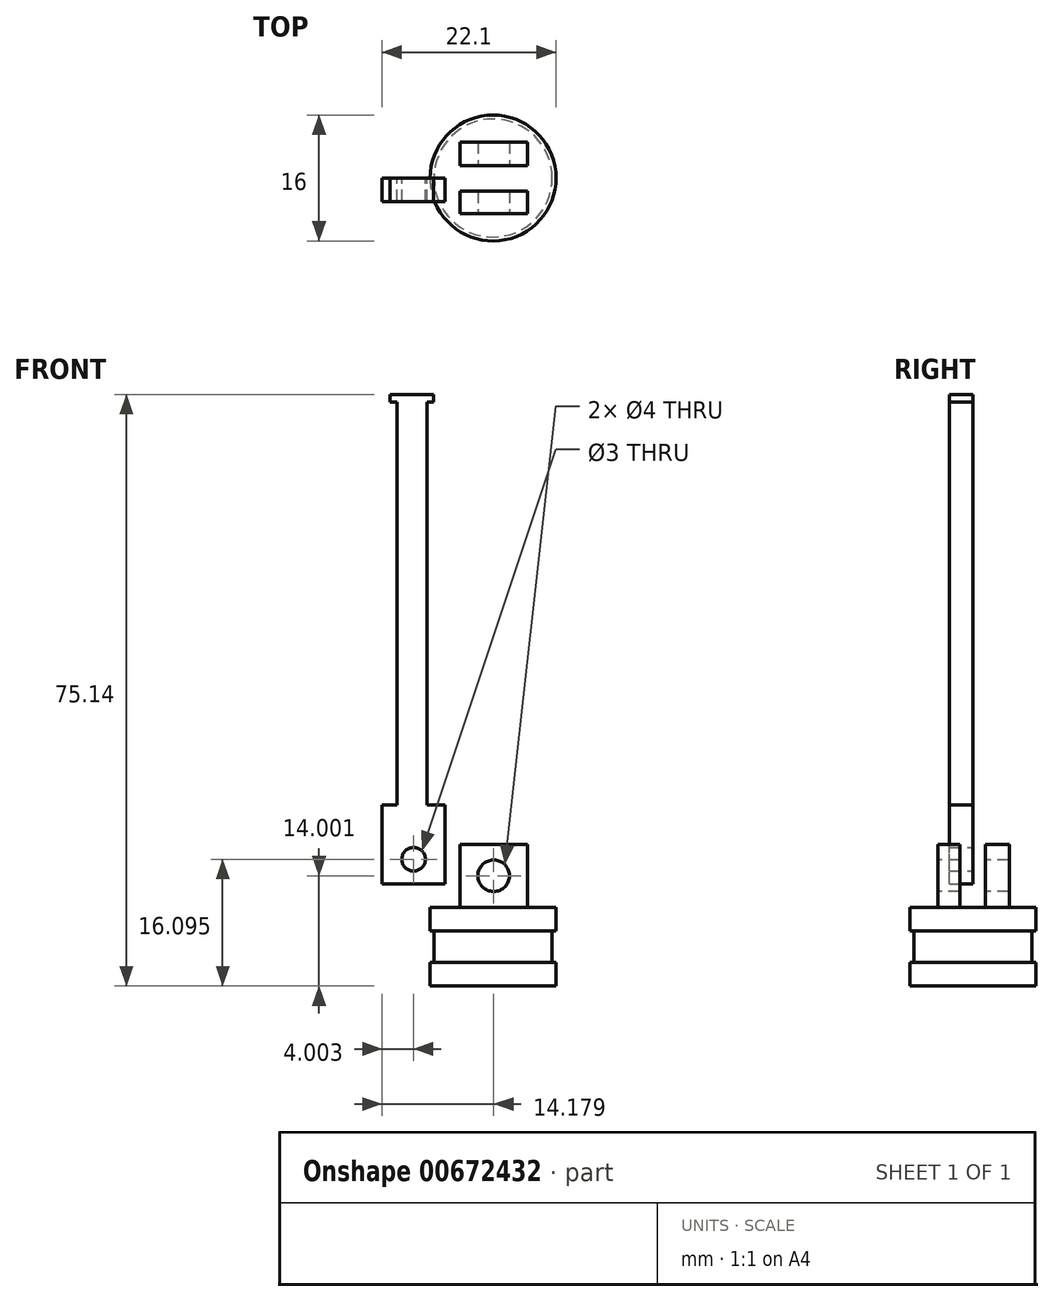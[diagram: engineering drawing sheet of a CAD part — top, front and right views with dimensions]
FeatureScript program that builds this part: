
annotation { "Feature Type Name" : "Feature", "Feature Type Description" : "" }
export const myFeature = defineFeature(function(context is Context, id is Id, definition is map)
    precondition{}
    {
        {
            var Q0;
            Q0=qCreatedBy(makeId("Front.planeOp"),FACE);
            var sketch = newSketch(context, id + "F0", { "sketchPlane" : qUnion([Q0])});
            skLineSegment(sketch, "E0", {"start": v(0, 8.53) * mm, "end": v(-8, 8.53) * mm});
            skLineSegment(sketch, "E1", {"start": v(-8, 8.53) * mm, "end": v(-8, 5.53) * mm});
            skLineSegment(sketch, "E2", {"start": v(-8, 5.53) * mm, "end": v(-7.5, 5.53) * mm});
            skLineSegment(sketch, "E3", {"start": v(-7.5, 5.53) * mm, "end": v(-7.5, 1.53) * mm});
            skLineSegment(sketch, "E4", {"start": v(-7.5, 1.53) * mm, "end": v(-8, 1.53) * mm});
            skLineSegment(sketch, "E5", {"start": v(-8, 1.53) * mm, "end": v(-8, -1.47) * mm});
            skLineSegment(sketch, "E6", {"start": v(-8, -1.47) * mm, "end": v(0, -1.47) * mm});
            skLineSegment(sketch, "E7", {"start": v(0, -1.47) * mm, "end": v(0, 8.53) * mm});
            skSolve(sketch);
        }
        {
            var Q0;
            Q0=makeQuery(id+"F0.imprint","IMPRINT",FACE,{"disambiguationData":[TD([[makeQuery(id+"F0.imprint","IMPRINT",EDGE,{"derivedFrom":sQuery(id+"F0.wireOp",EDGE,"E0")}),1.0]])]});
            var Q1;
            Q1=sQuery(id+"F0.wireOp",EDGE,"E7");
            revolve(context, id + "F1", {"entities" : qUnion([Q0]), "axis" : qUnion([Q1]), "revolveType" : RevolveType.FULL});
        }
        {
            var Q0;
            Q0=makeQuery(id+"F1.opRevolve","SWEPT_FACE",FACE,{"disambiguationData":[OSD([sQuery(id+"F0.wireOp",EDGE,"E0")])]});
            var sketch = newSketch(context, id + "F2", { "sketchPlane" : qUnion([Q0])});
            skLineSegment(sketch, "E8.bottom", {"start": v(-3, -4.5) * mm, "end": v(6, -4.5) * mm});
            skLineSegment(sketch, "E8.top", {"start": v(-2.71, 4.59) * mm, "end": v(6, 4.59) * mm});
            skLineSegment(sketch, "E9", {"start": v(-3, -1.67) * mm, "end": v(6, -1.67) * mm});
            skLineSegment(sketch, "E10", {"start": v(-2.71, 1.59) * mm, "end": v(6, 1.59) * mm});
            skLineSegment(sketch, "E11", {"start": v(4.37, -4.5) * mm, "end": v(4.37, -1.67) * mm});
            skLineSegment(sketch, "E12", {"start": v(4.37, 1.59) * mm, "end": v(4.37, 4.59) * mm});
            skLineSegment(sketch, "E13", {"start": v(-2.71, 4.59) * mm, "end": v(-4.21, 4.59) * mm});
            skLineSegment(sketch, "E14", {"start": v(-4.21, 4.59) * mm, "end": v(-4.21, 1.59) * mm});
            skLineSegment(sketch, "E15", {"start": v(-4.21, 1.59) * mm, "end": v(-2.71, 1.59) * mm});
            skLineSegment(sketch, "E16", {"start": v(-3, -1.67) * mm, "end": v(-4.21, -1.67) * mm});
            skLineSegment(sketch, "E17", {"start": v(-4.21, -1.67) * mm, "end": v(-4.21, -4.5) * mm});
            skLineSegment(sketch, "E18", {"start": v(-4.21, -4.5) * mm, "end": v(-3, -4.5) * mm});
            skSolve(sketch);
        }
        {
            var Q0;
            Q0=makeQuery(id+"F2.imprint","IMPRINT",FACE,{"disambiguationData":[TD([[makeQuery(id+"F2.imprint","IMPRINT",EDGE,{"derivedFrom":sQuery(id+"F2.wireOp",EDGE,"E8.bottom")}),1.0]])]});
            var Q1;
            {var subQ0=sQuery(id+"F2.wireOp",EDGE,"E8.top");Q1=makeQuery(id+"F2.imprint","IMPRINT",FACE,{"disambiguationData":[TD([[makeQuery(id+"F2.imprint","IMPRINT",EDGE,{"derivedFrom":subQ0}),-1.0]])]});}
            extrude(context, id + "F3", {"entities" : qUnion([Q0, Q1]), "operationType" : NewBodyOperationType.ADD, "depth" : 8 * mm, "offsetDistance" : 25 * mm});
        }
        {
            var Q0;
            Q0=makeQuery(id+"F3.opExtrude","SWEPT_FACE",FACE,{"disambiguationData":[OSD([sQuery(id+"F2.wireOp",EDGE,"E8.bottom")])]});
            var sketch = newSketch(context, id + "F4", { "sketchPlane" : qUnion([Q0])});
            skPoint(sketch, "E19", {"position": v(0.08, 12.53) * mm});
            skPoint(sketch, "E19.positionSnap0", {"position": v(0.08, 16.53) * mm});
            skPoint(sketch, "E19.positionSnap1", {"position": v(4.37, 12.53) * mm});
            skSolve(sketch);
        }
        {
            var Q0;
            Q0=sQuery(id+"F4.wireOp",VERTEX,"E19");
            var Q1;
            Q1=makeQuery(id+"F1.opRevolve","SWEPT_BODY",BODY,{"disambiguationData":[OSD([sQuery(id+"F0.wireOp",EDGE,"E0"),sQuery(id+"F0.wireOp",EDGE,"E1"),sQuery(id+"F0.wireOp",EDGE,"E2"),sQuery(id+"F0.wireOp",EDGE,"E3"),sQuery(id+"F0.wireOp",EDGE,"E4"),sQuery(id+"F0.wireOp",EDGE,"E5"),sQuery(id+"F0.wireOp",EDGE,"E6"),sQuery(id+"F0.wireOp",EDGE,"E7")])]});
            hole(context, id + "F5", {"style" : HoleStyle.SIMPLE, "endStyle" : HoleEndStyle.THROUGH, "holeDiameter" : 4 * mm, "majorDiameter" : 5 * mm, "isTappedThrough" : true, "tappedDepth" : 12 * mm, "tapClearance" : 3, "startFromSketch" : true, "locations" : qUnion([Q0]), "scope" : qUnion([Q1])});
        }
        {
            var Q0;
            Q0=qCreatedBy(makeId("Front.planeOp"),FACE);
            var sketch = newSketch(context, id + "F6", { "sketchPlane" : qUnion([Q0])});
            skLineSegment(sketch, "E20.bottom", {"start": v(-6.1, 11.52) * mm, "end": v(-14.1, 11.52) * mm});
            skLineSegment(sketch, "E20.top", {"start": v(-6.1, 21.52) * mm, "end": v(-14.1, 21.52) * mm});
            skLineSegment(sketch, "E20.left", {"start": v(-6.1, 11.52) * mm, "end": v(-6.1, 21.52) * mm});
            skLineSegment(sketch, "E20.right", {"start": v(-14.1, 11.52) * mm, "end": v(-14.1, 21.52) * mm});
            skPoint(sketch, "E21", {"position": v(-10.1, 16.52) * mm});
            skPoint(sketch, "E21.positionSnap0", {"position": v(-10.1, 11.52) * mm});
            skPoint(sketch, "E21.positionSnap1", {"position": v(-6.1, 16.52) * mm});
            skLineSegment(sketch, "E22", {"start": v(-8.42, 21.52) * mm, "end": v(-8.42, 72.7) * mm});
            skLineSegment(sketch, "E23", {"start": v(-8.42, 72.7) * mm, "end": v(-12.2, 72.7) * mm});
            skLineSegment(sketch, "E24", {"start": v(-12.2, 72.7) * mm, "end": v(-12.2, 21.52) * mm});
            skLineSegment(sketch, "E25.bottom", {"start": v(-8.42, 72.7) * mm, "end": v(-13.12, 72.7) * mm});
            skLineSegment(sketch, "E25.top", {"start": v(-8.42, 73.67) * mm, "end": v(-13.12, 73.67) * mm});
            skLineSegment(sketch, "E25.left", {"start": v(-8.42, 72.7) * mm, "end": v(-8.42, 73.67) * mm});
            skLineSegment(sketch, "E25.right", {"start": v(-13.12, 72.7) * mm, "end": v(-13.12, 73.67) * mm});
            skLineSegment(sketch, "E26.bottom", {"start": v(-8.42, 72.7) * mm, "end": v(-7.57, 72.7) * mm});
            skLineSegment(sketch, "E26.top", {"start": v(-8.42, 73.67) * mm, "end": v(-7.57, 73.67) * mm});
            skLineSegment(sketch, "E26.right", {"start": v(-7.57, 72.7) * mm, "end": v(-7.57, 73.67) * mm});
            skSolve(sketch);
        }
        {
            var Q0;
            Q0 = qSketchRegion(id + "F6", true);
            extrude(context, id + "F7", {"entities" : qUnion([Q0]), "depth" : 3 * mm, "offsetDistance" : 25 * mm});
        }
        {
            var Q0;
            Q0=makeQuery(id+"F7.opExtrude","CAP_FACE",FACE,{"disambiguationData":[OSD([sQuery(id+"F6.wireOp",EDGE,"E20.bottom"),sQuery(id+"F6.wireOp",EDGE,"E20.top"),sQuery(id+"F6.wireOp",EDGE,"E20.left"),sQuery(id+"F6.wireOp",EDGE,"E20.right"),sQuery(id+"F6.wireOp",EDGE,"E22"),sQuery(id+"F6.wireOp",EDGE,"E24"),sQuery(id+"F6.wireOp",EDGE,"E25.bottom"),sQuery(id+"F6.wireOp",EDGE,"E25.top"),sQuery(id+"F6.wireOp",EDGE,"E25.right"),sQuery(id+"F6.wireOp",EDGE,"E26.bottom"),sQuery(id+"F6.wireOp",EDGE,"E26.top"),sQuery(id+"F6.wireOp",EDGE,"E26.right")])],"isStart":true});
            var sketch = newSketch(context, id + "F8", { "sketchPlane" : qUnion([Q0])});
            skPoint(sketch, "E27", {"position": v(10.1, 16.52) * mm});
            skPoint(sketch, "E27.positionSnap0", {"position": v(10.1, 11.52) * mm});
            skPoint(sketch, "E27.positionSnap1", {"position": v(6.1, 16.52) * mm});
            skPoint(sketch, "E28", {"position": v(10.1, 14.63) * mm});
            skSolve(sketch);
        }
        {
            var Q0;
            Q0=sQuery(id+"F8.wireOp",VERTEX,"E28");
            var Q1;
            Q1=makeQuery(id+"F7.opExtrude","SWEPT_BODY",BODY,{"disambiguationData":[OSD([sQuery(id+"F6.wireOp",EDGE,"E20.bottom"),sQuery(id+"F6.wireOp",EDGE,"E20.top"),sQuery(id+"F6.wireOp",EDGE,"E20.left"),sQuery(id+"F6.wireOp",EDGE,"E20.right"),sQuery(id+"F6.wireOp",EDGE,"E22"),sQuery(id+"F6.wireOp",EDGE,"E24"),sQuery(id+"F6.wireOp",EDGE,"E25.bottom"),sQuery(id+"F6.wireOp",EDGE,"E25.top"),sQuery(id+"F6.wireOp",EDGE,"E25.right"),sQuery(id+"F6.wireOp",EDGE,"E26.bottom"),sQuery(id+"F6.wireOp",EDGE,"E26.top"),sQuery(id+"F6.wireOp",EDGE,"E26.right")])]});
            hole(context, id + "F9", {"style" : HoleStyle.SIMPLE, "endStyle" : HoleEndStyle.THROUGH, "holeDiameter" : 3 * mm, "majorDiameter" : 5 * mm, "isTappedThrough" : true, "tappedDepth" : 12 * mm, "tapClearance" : 3, "startFromSketch" : true, "locations" : qUnion([Q0]), "scope" : qUnion([Q1])});
        }
    });
